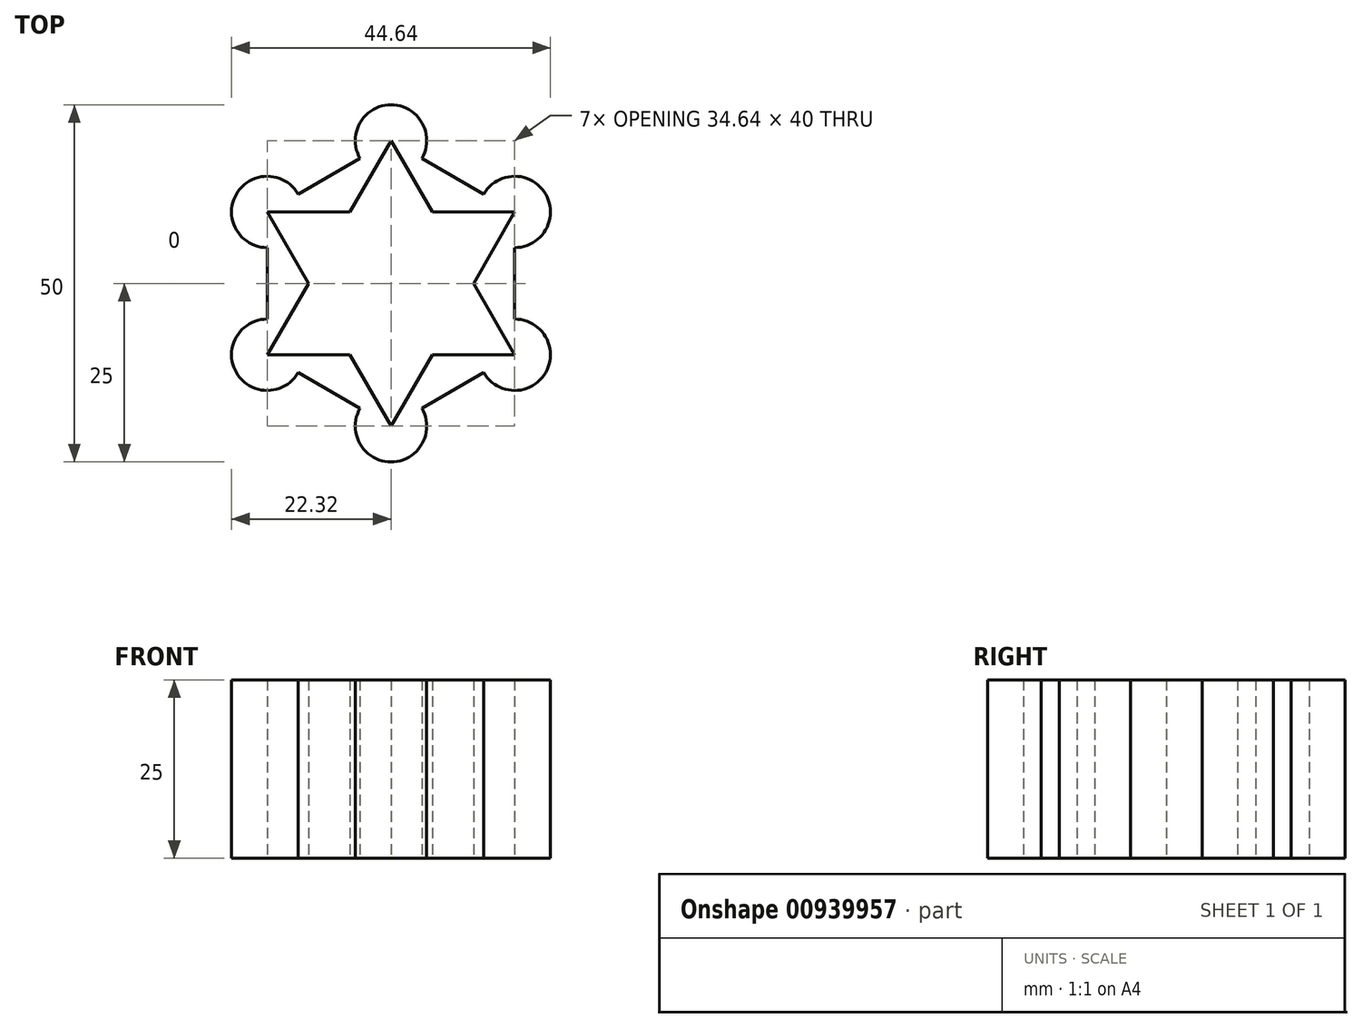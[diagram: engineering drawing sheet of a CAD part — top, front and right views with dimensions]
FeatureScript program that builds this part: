
annotation { "Feature Type Name" : "Feature", "Feature Type Description" : "" }
export const myFeature = defineFeature(function(context is Context, id is Id, definition is map)
    precondition{}
    {
        {
            var Q0;
            Q0=qCreatedBy(makeId("Top.planeOp"),FACE);
            var sketch = newSketch(context, id + "F0", { "sketchPlane" : qUnion([Q0])});
            skCircle(sketch, "E0", {"center": v(0, 0) * mm, "radius": 5 * mm});
            skCircle(sketch, "E1", {"center": v(0, 10) * mm, "radius": 5 * mm});
            skCircle(sketch, "E2.1.0", {"center": v(-8.66, 5) * mm, "radius": 5 * mm});
            skCircle(sketch, "E2.2.0", {"center": v(-8.66, -5) * mm, "radius": 5 * mm});
            skCircle(sketch, "E2.3.0", {"center": v(0, -10) * mm, "radius": 5 * mm});
            skCircle(sketch, "E2.4.0", {"center": v(8.66, -5) * mm, "radius": 5 * mm});
            skCircle(sketch, "E2.5.0", {"center": v(8.66, 5) * mm, "radius": 5 * mm});
            skCircle(sketch, "E3", {"center": v(0, 20) * mm, "radius": 5 * mm});
            skCircle(sketch, "E4.1.0", {"center": v(-17.32, 10) * mm, "radius": 5 * mm});
            skCircle(sketch, "E4.2.0", {"center": v(-17.32, -10) * mm, "radius": 5 * mm});
            skCircle(sketch, "E4.3.0", {"center": v(0, -20) * mm, "radius": 5 * mm});
            skCircle(sketch, "E4.4.0", {"center": v(17.32, -10) * mm, "radius": 5 * mm});
            skCircle(sketch, "E4.5.0", {"center": v(17.32, 10) * mm, "radius": 5 * mm});
            skLineSegment(sketch, "E5", {"start": v(-17.32, 10) * mm, "end": v(0, 20) * mm});
            skLineSegment(sketch, "E6", {"start": v(0, 20) * mm, "end": v(17.32, 10) * mm});
            skLineSegment(sketch, "E7", {"start": v(17.32, 10) * mm, "end": v(17.32, -10) * mm});
            skLineSegment(sketch, "E8", {"start": v(17.32, -10) * mm, "end": v(0, -20) * mm});
            skLineSegment(sketch, "E9", {"start": v(0, -20) * mm, "end": v(-17.32, -10) * mm});
            skLineSegment(sketch, "E10", {"start": v(-17.32, -10) * mm, "end": v(-17.32, 10) * mm});
            skLineSegment(sketch, "E11", {"start": v(-17.32, 10) * mm, "end": v(17.32, -10) * mm});
            skLineSegment(sketch, "E12", {"start": v(17.32, 10) * mm, "end": v(-17.32, -10) * mm});
            skLineSegment(sketch, "E13", {"start": v(0, 20) * mm, "end": v(0, -20) * mm});
            skLineSegment(sketch, "E14", {"start": v(-8.66, 5) * mm, "end": v(0, 10) * mm});
            skLineSegment(sketch, "E15", {"start": v(0, 10) * mm, "end": v(8.66, 5) * mm});
            skLineSegment(sketch, "E16", {"start": v(8.66, 5) * mm, "end": v(8.66, -5) * mm});
            skLineSegment(sketch, "E17", {"start": v(8.66, -5) * mm, "end": v(0, -10) * mm});
            skLineSegment(sketch, "E18", {"start": v(0, -10) * mm, "end": v(-8.66, -5) * mm});
            skLineSegment(sketch, "E19", {"start": v(-8.66, -5) * mm, "end": v(-8.66, 5) * mm});
            skLineSegment(sketch, "E20", {"start": v(0, 20) * mm, "end": v(-8.66, 5) * mm});
            skLineSegment(sketch, "E21", {"start": v(0, 20) * mm, "end": v(-17.32, -10) * mm});
            skLineSegment(sketch, "E22", {"start": v(0, 20) * mm, "end": v(-8.66, -5) * mm});
            skLineSegment(sketch, "E23", {"start": v(0, 20) * mm, "end": v(8.66, -5) * mm});
            skLineSegment(sketch, "E24", {"start": v(0, 20) * mm, "end": v(17.32, -10) * mm});
            skLineSegment(sketch, "E25", {"start": v(17.32, 10) * mm, "end": v(-17.32, 10) * mm});
            skLineSegment(sketch, "E26", {"start": v(17.32, 10) * mm, "end": v(-8.66, 5) * mm});
            skLineSegment(sketch, "E27", {"start": v(17.32, 10) * mm, "end": v(0, -10) * mm});
            skLineSegment(sketch, "E28", {"start": v(17.32, 10) * mm, "end": v(0, -20) * mm});
            skLineSegment(sketch, "E29", {"start": v(17.32, -10) * mm, "end": v(-17.32, -10) * mm});
            skLineSegment(sketch, "E30", {"start": v(17.32, -10) * mm, "end": v(-8.66, -5) * mm});
            skLineSegment(sketch, "E31", {"start": v(17.32, -10) * mm, "end": v(0, 10) * mm});
            skLineSegment(sketch, "E32", {"start": v(0, -20) * mm, "end": v(-17.32, 10) * mm});
            skLineSegment(sketch, "E33", {"start": v(-17.32, -10) * mm, "end": v(8.66, -5) * mm});
            skLineSegment(sketch, "E34", {"start": v(-17.32, -10) * mm, "end": v(0, 10) * mm});
            skLineSegment(sketch, "E35", {"start": v(0, -10) * mm, "end": v(-17.32, 10) * mm});
            skLineSegment(sketch, "E36", {"start": v(-17.32, 10) * mm, "end": v(8.66, 5) * mm});
            skLineSegment(sketch, "E37", {"start": v(0, -20) * mm, "end": v(8.66, 5) * mm});
            skLineSegment(sketch, "E38", {"start": v(0, -20) * mm, "end": v(-8.66, 5) * mm});
            skLineSegment(sketch, "E39", {"start": v(-8.66, 5) * mm, "end": v(8.66, 5) * mm});
            skLineSegment(sketch, "E40", {"start": v(-8.66, -5) * mm, "end": v(8.66, -5) * mm});
            skSolve(sketch);
        }
        {
            var Q0;
            Q0 = qSketchRegion(id + "F0", true);
            extrude(context, id + "F1", {"entities" : qUnion([Q0]), "depth" : 25 * mm, "offsetDistance" : 25 * mm});
        }
    });
